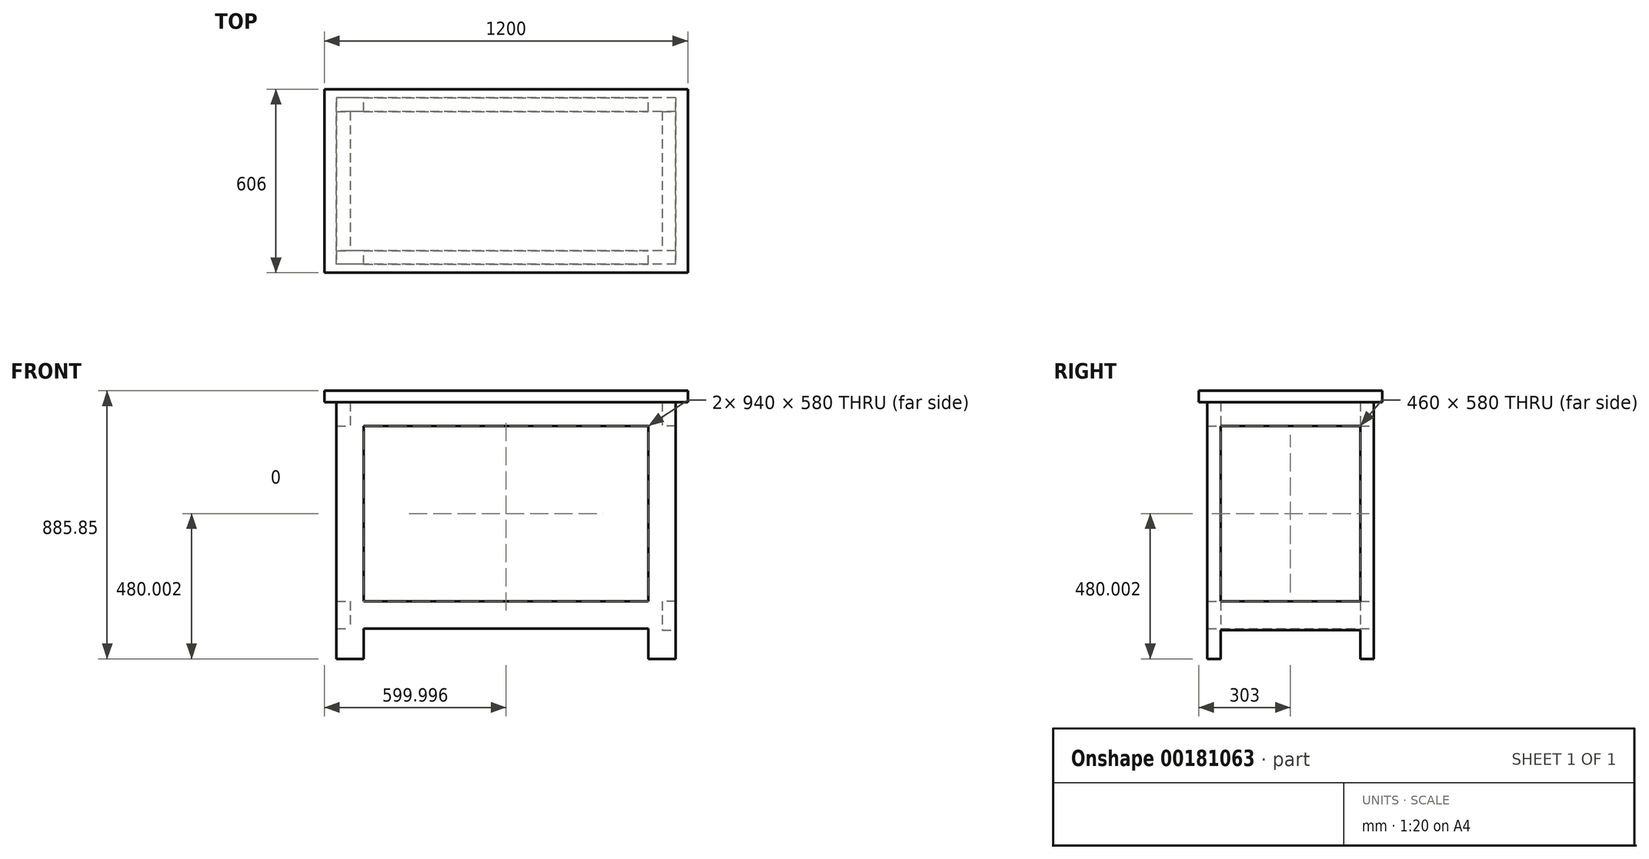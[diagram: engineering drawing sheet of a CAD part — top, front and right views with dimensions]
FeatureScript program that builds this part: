
annotation { "Feature Type Name" : "Feature", "Feature Type Description" : "" }
export const myFeature = defineFeature(function(context is Context, id is Id, definition is map)
    precondition{}
    {
        {
            var Q0;
            Q0=qCreatedBy(makeId("Front.planeOp"),FACE);
            var sketch = newSketch(context, id + "F0", { "sketchPlane" : qUnion([Q0])});
            skLineSegment(sketch, "E0.bottom", {"start": v(-430.18, 12.15) * mm, "end": v(509.82, 12.15) * mm});
            skLineSegment(sketch, "E0.top", {"start": v(-430.18, -77.85) * mm, "end": v(509.82, -77.85) * mm});
            skLineSegment(sketch, "E0.left", {"start": v(-430.18, 12.15) * mm, "end": v(-430.18, -77.85) * mm});
            skLineSegment(sketch, "E0.right", {"start": v(509.82, 12.15) * mm, "end": v(509.82, -77.85) * mm});
            skLineSegment(sketch, "E1.bottom", {"start": v(-430.18, -657.85) * mm, "end": v(509.82, -657.85) * mm});
            skLineSegment(sketch, "E1.top", {"start": v(-430.18, -747.85) * mm, "end": v(509.82, -747.85) * mm});
            skLineSegment(sketch, "E1.left", {"start": v(-430.18, -657.85) * mm, "end": v(-430.18, -747.85) * mm});
            skLineSegment(sketch, "E1.right", {"start": v(509.82, -657.85) * mm, "end": v(509.82, -747.85) * mm});
            skLineSegment(sketch, "E2.bottom", {"start": v(-430.18, 12.15) * mm, "end": v(-520.18, 12.15) * mm});
            skLineSegment(sketch, "E2.top", {"start": v(-430.18, -847.85) * mm, "end": v(-520.18, -847.85) * mm});
            skLineSegment(sketch, "E2.left", {"start": v(-430.18, 12.15) * mm, "end": v(-430.18, -847.85) * mm});
            skLineSegment(sketch, "E2.right", {"start": v(-520.18, 12.15) * mm, "end": v(-520.18, -847.85) * mm});
            skLineSegment(sketch, "E3.bottom", {"start": v(599.82, 12.15) * mm, "end": v(509.82, 12.15) * mm});
            skLineSegment(sketch, "E3.top", {"start": v(599.82, -847.85) * mm, "end": v(509.82, -847.85) * mm});
            skLineSegment(sketch, "E3.left", {"start": v(599.82, 12.15) * mm, "end": v(599.82, -847.85) * mm});
            skLineSegment(sketch, "E3.right", {"start": v(509.82, 12.15) * mm, "end": v(509.82, -847.85) * mm});
            skSolve(sketch);
        }
        {
            var Q0;
            Q0 = qSketchRegion(id + "F0", true);
            extrude(context, id + "F1", {"entities" : qUnion([Q0]), "depth" : 45 * mm});
        }
        {
            var Q0;
            Q0=qCreatedBy(makeId("Front.planeOp"),FACE);
            cPlane(context, id + "F2", {"entities" : qUnion([Q0]), "cplaneType" : CPlaneType.OFFSET, "offset" : 45 * mm, "width" : 150 * mm, "height" : 150 * mm});
        }
        {
            var Q0;
            Q0=qCreatedBy(id+"F2.planeOp",FACE);
            var sketch = newSketch(context, id + "F3", { "sketchPlane" : qUnion([Q0])});
            skLineSegment(sketch, "E4.bottom", {"start": v(-520.18, 12.15) * mm, "end": v(-475.18, 12.15) * mm});
            skLineSegment(sketch, "E4.top", {"start": v(-520.18, -77.85) * mm, "end": v(-475.18, -77.85) * mm});
            skLineSegment(sketch, "E4.left", {"start": v(-520.18, 12.15) * mm, "end": v(-520.18, -77.85) * mm});
            skLineSegment(sketch, "E4.right", {"start": v(-475.18, 12.15) * mm, "end": v(-475.18, -77.85) * mm});
            skLineSegment(sketch, "E5.bottom", {"start": v(599.82, 12.15) * mm, "end": v(554.82, 12.15) * mm});
            skLineSegment(sketch, "E5.top", {"start": v(599.82, -77.85) * mm, "end": v(554.82, -77.85) * mm});
            skLineSegment(sketch, "E5.left", {"start": v(599.82, 12.15) * mm, "end": v(599.82, -77.85) * mm});
            skLineSegment(sketch, "E5.right", {"start": v(554.82, 12.15) * mm, "end": v(554.82, -77.85) * mm});
            skLineSegment(sketch, "E6.bottom", {"start": v(599.82, -657.85) * mm, "end": v(554.82, -657.85) * mm});
            skLineSegment(sketch, "E6.top", {"start": v(554.82, -752.85) * mm, "end": v(599.82, -752.85) * mm});
            skLineSegment(sketch, "E6.left", {"start": v(599.82, -657.85) * mm, "end": v(599.82, -752.85) * mm});
            skLineSegment(sketch, "E6.right", {"start": v(554.82, -657.85) * mm, "end": v(554.82, -752.85) * mm});
            skLineSegment(sketch, "E7.bottom", {"start": v(-520.18, -657.85) * mm, "end": v(-475.18, -657.85) * mm});
            skLineSegment(sketch, "E7.top", {"start": v(-520.18, -747.85) * mm, "end": v(-475.18, -747.85) * mm});
            skLineSegment(sketch, "E7.left", {"start": v(-520.18, -657.85) * mm, "end": v(-520.18, -747.85) * mm});
            skLineSegment(sketch, "E7.right", {"start": v(-475.18, -657.85) * mm, "end": v(-475.18, -747.85) * mm});
            skSolve(sketch);
        }
        {
            var Q0;
            Q0 = qSketchRegion(id + "F3", true);
            extrude(context, id + "F4", {"entities" : qUnion([Q0]), "operationType" : NewBodyOperationType.ADD, "depth" : 460 * mm});
        }
        {
            var Q0;
            Q0=qCreatedBy(id+"F2.planeOp",FACE);
            cPlane(context, id + "F5", {"entities" : qUnion([Q0]), "cplaneType" : CPlaneType.OFFSET, "offset" : 460 * mm, "width" : 150 * mm, "height" : 150 * mm});
        }
        {
            var Q0;
            Q0=qCreatedBy(id+"F5.planeOp",FACE);
            var sketch = newSketch(context, id + "F6", { "sketchPlane" : qUnion([Q0])});
            skLineSegment(sketch, "E8.bottom", {"start": v(-430.18, 12.15) * mm, "end": v(509.82, 12.15) * mm});
            skLineSegment(sketch, "E8.top", {"start": v(-430.18, -77.85) * mm, "end": v(509.82, -77.85) * mm});
            skLineSegment(sketch, "E8.left", {"start": v(-430.18, 12.15) * mm, "end": v(-430.18, -77.85) * mm});
            skLineSegment(sketch, "E8.right", {"start": v(509.82, 12.15) * mm, "end": v(509.82, -77.85) * mm});
            skLineSegment(sketch, "E9.bottom", {"start": v(-430.18, -657.85) * mm, "end": v(509.82, -657.85) * mm});
            skLineSegment(sketch, "E9.top", {"start": v(-430.18, -747.85) * mm, "end": v(509.82, -747.85) * mm});
            skLineSegment(sketch, "E9.left", {"start": v(-430.18, -657.85) * mm, "end": v(-430.18, -747.85) * mm});
            skLineSegment(sketch, "E9.right", {"start": v(509.82, -657.85) * mm, "end": v(509.82, -747.85) * mm});
            skLineSegment(sketch, "E10.bottom", {"start": v(-430.18, 12.15) * mm, "end": v(-520.18, 12.15) * mm});
            skLineSegment(sketch, "E10.top", {"start": v(-430.18, -847.85) * mm, "end": v(-520.18, -847.85) * mm});
            skLineSegment(sketch, "E10.left", {"start": v(-430.18, 12.15) * mm, "end": v(-430.18, -847.85) * mm});
            skLineSegment(sketch, "E10.right", {"start": v(-520.18, 12.15) * mm, "end": v(-520.18, -847.85) * mm});
            skLineSegment(sketch, "E11.bottom", {"start": v(599.82, 12.15) * mm, "end": v(509.82, 12.15) * mm});
            skLineSegment(sketch, "E11.top", {"start": v(599.82, -847.85) * mm, "end": v(509.82, -847.85) * mm});
            skLineSegment(sketch, "E11.left", {"start": v(599.82, 12.15) * mm, "end": v(599.82, -847.85) * mm});
            skLineSegment(sketch, "E11.right", {"start": v(509.82, 12.15) * mm, "end": v(509.82, -847.85) * mm});
            skSolve(sketch);
        }
        {
            var Q0;
            Q0 = qSketchRegion(id + "F6", true);
            extrude(context, id + "F7", {"entities" : qUnion([Q0]), "operationType" : NewBodyOperationType.ADD, "depth" : 45 * mm});
        }
        {
            var Q0;
            Q0=qCreatedBy(makeId("Top.planeOp"),FACE);
            var sketch = newSketch(context, id + "F8", { "sketchPlane" : qUnion([Q0])});
            skLineSegment(sketch, "E12.bottom", {"start": v(-560.18, 28) * mm, "end": v(639.82, 28) * mm});
            skLineSegment(sketch, "E12.top", {"start": v(-560.18, -578) * mm, "end": v(639.82, -578) * mm});
            skLineSegment(sketch, "E12.left", {"start": v(-560.18, 28) * mm, "end": v(-560.18, -578) * mm});
            skLineSegment(sketch, "E12.right", {"start": v(639.82, 28) * mm, "end": v(639.82, -578) * mm});
            skSolve(sketch);
        }
        {
            var Q0;
            Q0 = qSketchRegion(id + "F8", true);
            extrude(context, id + "F9", {"entities" : qUnion([Q0]), "operationType" : NewBodyOperationType.ADD, "depth" : 19 * mm});
        }
        {
            var Q0;
            Q0=qCreatedBy(makeId("Top.planeOp"),FACE);
            cPlane(context, id + "F10", {"entities" : qUnion([Q0]), "cplaneType" : CPlaneType.OFFSET, "offset" : 19 * mm, "width" : 150 * mm, "height" : 150 * mm});
        }
        {
            var Q0;
            Q0=qCreatedBy(id+"F10.planeOp",FACE);
            var sketch = newSketch(context, id + "F11", { "sketchPlane" : qUnion([Q0])});
            skLineSegment(sketch, "E13.bottom", {"start": v(-560.18, 28) * mm, "end": v(639.82, 28) * mm});
            skLineSegment(sketch, "E13.top", {"start": v(-560.18, -578) * mm, "end": v(639.82, -578) * mm});
            skLineSegment(sketch, "E13.left", {"start": v(-560.18, 28) * mm, "end": v(-560.18, -578) * mm});
            skLineSegment(sketch, "E13.right", {"start": v(639.82, 28) * mm, "end": v(639.82, -578) * mm});
            skSolve(sketch);
        }
        {
            var Q0;
            Q0 = qSketchRegion(id + "F11", true);
            extrude(context, id + "F12", {"entities" : qUnion([Q0]), "operationType" : NewBodyOperationType.ADD, "depth" : 19 * mm});
        }
    });
